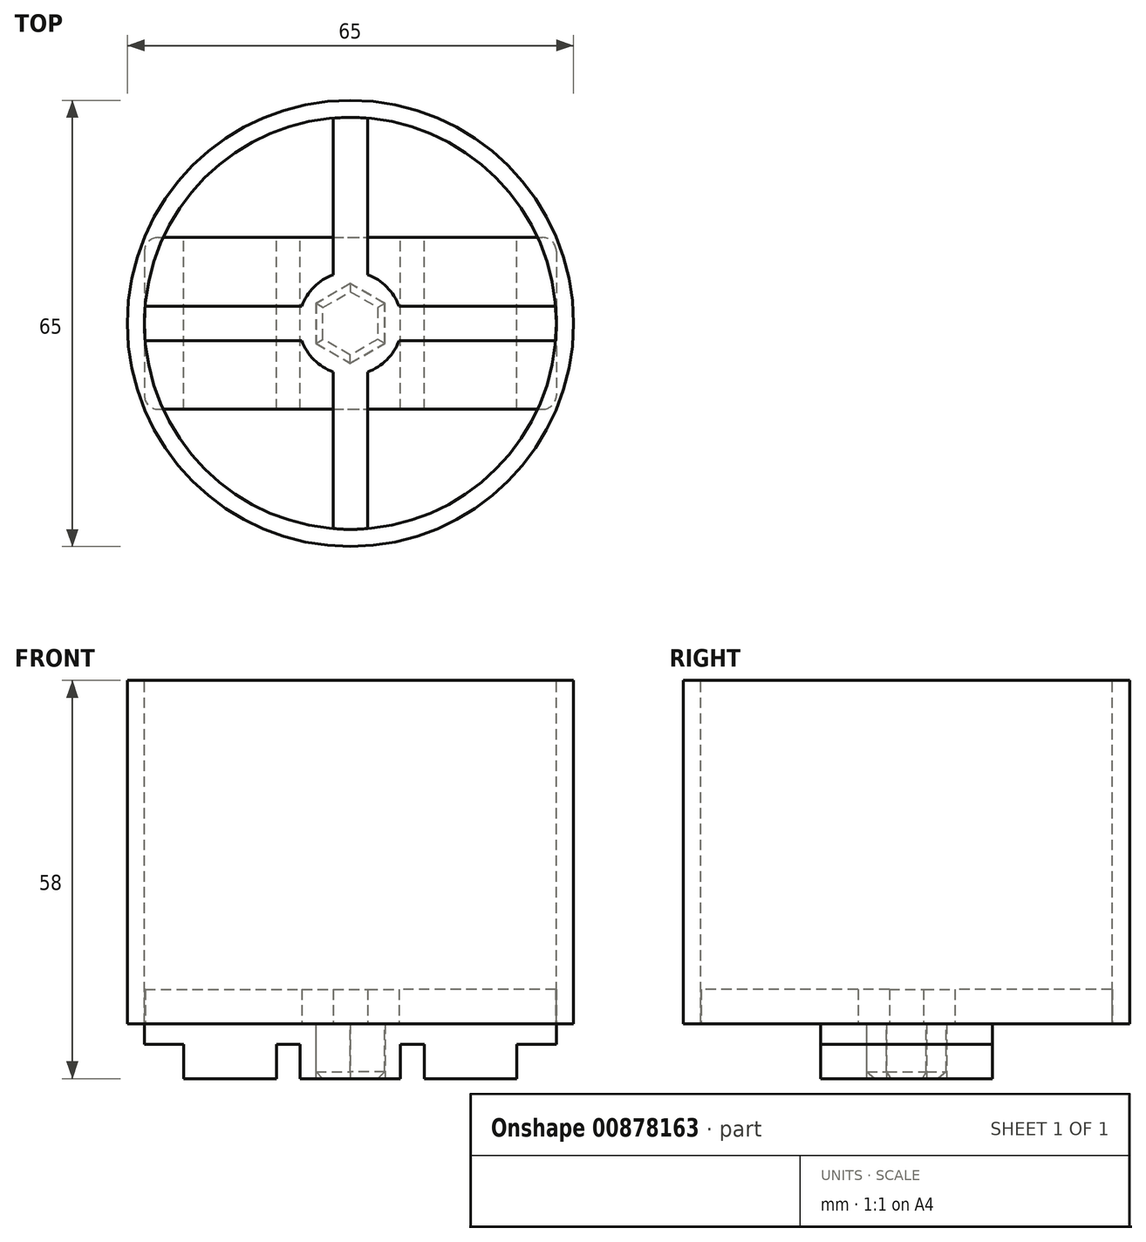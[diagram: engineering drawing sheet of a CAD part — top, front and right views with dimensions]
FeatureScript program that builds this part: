
annotation { "Feature Type Name" : "Feature", "Feature Type Description" : "" }
export const myFeature = defineFeature(function(context is Context, id is Id, definition is map)
    precondition{}
    {
        {
            var Q0;
            Q0=qCreatedBy(makeId("Top.planeOp"),FACE);
            var sketch = newSketch(context, id + "F0", { "sketchPlane" : qUnion([Q0])});
            skLineSegment(sketch, "E0.bottom", {"start": v(-30, 12.5) * mm, "end": v(30, 12.5) * mm});
            skLineSegment(sketch, "E0.top", {"start": v(-30, -12.5) * mm, "end": v(30, -12.5) * mm});
            skLineSegment(sketch, "E0.left", {"start": v(-30, 12.5) * mm, "end": v(-30, -12.5) * mm});
            skLineSegment(sketch, "E0.right", {"start": v(30, 12.5) * mm, "end": v(30, -12.5) * mm});
            skPoint(sketch, "E1", {"position": v(-30, 0) * mm});
            skPoint(sketch, "E2", {"position": v(0, 12.5) * mm});
            skSolve(sketch);
        }
        {
            var Q0;
            Q0=makeQuery(id+"F0.imprint","IMPRINT",FACE,{"disambiguationData":[TD([[makeQuery(id+"F0.imprint","IMPRINT",EDGE,{"derivedFrom":sQuery(id+"F0.wireOp",EDGE,"E0.bottom")}),-1.0]])]});
            extrude(context, id + "F1", {"entities" : qUnion([Q0]), "oppositeDirection" : true, "depth" : 8 * mm, "offsetDistance" : 25 * mm});
        }
        {
            var Q0;
            Q0=makeQuery(id+"F1.opExtrude","CAP_FACE",FACE,{"disambiguationData":[OSD([sQuery(id+"F0.wireOp",EDGE,"E0.bottom"),sQuery(id+"F0.wireOp",EDGE,"E0.top"),sQuery(id+"F0.wireOp",EDGE,"E0.left"),sQuery(id+"F0.wireOp",EDGE,"E0.right")])],"isStart":false});
            var sketch = newSketch(context, id + "F2", { "sketchPlane" : qUnion([Q0])});
            skLineSegment(sketch, "E3.bottom", {"start": v(-24.25, 12.5) * mm, "end": v(-10.75, 12.5) * mm});
            skLineSegment(sketch, "E3.top", {"start": v(-24.25, -12.5) * mm, "end": v(-10.75, -12.5) * mm});
            skLineSegment(sketch, "E3.left", {"start": v(-24.25, 12.5) * mm, "end": v(-24.25, -12.5) * mm});
            skLineSegment(sketch, "E3.right", {"start": v(-10.75, 12.5) * mm, "end": v(-10.75, -12.5) * mm});
            skLineSegment(sketch, "E4.bottom", {"start": v(-7.3, 12.5) * mm, "end": v(7.3, 12.5) * mm});
            skLineSegment(sketch, "E4.top", {"start": v(-7.3, -12.5) * mm, "end": v(7.3, -12.5) * mm});
            skLineSegment(sketch, "E4.left", {"start": v(-7.3, 12.5) * mm, "end": v(-7.3, -12.5) * mm});
            skLineSegment(sketch, "E4.right", {"start": v(7.3, 12.5) * mm, "end": v(7.3, -12.5) * mm});
            skLineSegment(sketch, "E5.bottom", {"start": v(10.75, 12.5) * mm, "end": v(24.25, 12.5) * mm});
            skLineSegment(sketch, "E5.top", {"start": v(10.75, -12.5) * mm, "end": v(24.25, -12.5) * mm});
            skLineSegment(sketch, "E5.left", {"start": v(10.75, 12.5) * mm, "end": v(10.75, -12.5) * mm});
            skLineSegment(sketch, "E5.right", {"start": v(24.25, 12.5) * mm, "end": v(24.25, -12.5) * mm});
            skPoint(sketch, "E6", {"position": v(0, 12.5) * mm});
            skLineSegment(sketch, "E7", {"start": v(-10.75, 12.5) * mm, "end": v(-7.3, 12.5) * mm, "construction": true});
            skLineSegment(sketch, "E8", {"start": v(7.3, 12.5) * mm, "end": v(10.75, 12.5) * mm, "construction": true});
            skSolve(sketch);
        }
        {
            var Q0;
            {var subQ0=sQuery(id+"F2.wireOp",EDGE,"E3.left");Q0=makeQuery(id+"F2.imprint","IMPRINT",FACE,{"disambiguationData":[TD([[makeQuery(id+"F2.imprint","IMPRINT",EDGE,{"derivedFrom":subQ0}),-1.0]])]});}
            var Q1;
            {var subQ0=sQuery(id+"F2.wireOp",EDGE,"E3.right");Q1=makeQuery(id+"F2.imprint","IMPRINT",FACE,{"disambiguationData":[TD([[makeQuery(id+"F2.imprint","IMPRINT",EDGE,{"derivedFrom":subQ0}),1.0]])]});}
            var Q2;
            {var subQ0=sQuery(id+"F2.wireOp",EDGE,"E4.right");Q2=makeQuery(id+"F2.imprint","IMPRINT",FACE,{"disambiguationData":[TD([[makeQuery(id+"F2.imprint","IMPRINT",EDGE,{"derivedFrom":subQ0}),1.0]])]});}
            var Q3;
            {var subQ0=sQuery(id+"F2.wireOp",EDGE,"E5.right");Q3=makeQuery(id+"F2.imprint","IMPRINT",FACE,{"disambiguationData":[TD([[makeQuery(id+"F2.imprint","IMPRINT",EDGE,{"derivedFrom":subQ0}),1.0]])]});}
            extrude(context, id + "F3", {"entities" : qUnion([Q0, Q1, Q2, Q3]), "operationType" : NewBodyOperationType.REMOVE, "oppositeDirection" : true, "depth" : 5 * mm, "offsetDistance" : 25 * mm});
        }
        {
            var Q0;
            {var subQ0=sQuery(id+"F0.wireOp",EDGE,"E0.bottom");var subQ1=sQuery(id+"F0.wireOp",EDGE,"E0.top");Q0=makeQuery(id+"F3.boolean.opBoolean","SPLIT",FACE,{"disambiguationData":[TD([makeQuery(id+"F3.opExtrude","SWEPT_FACE",FACE,{"disambiguationData":[OSD([sQuery(id+"F2.wireOp",EDGE,"E4.left")])]})])],"derivedFrom":makeQuery(id+"F1.opExtrude","CAP_FACE",FACE,{"disambiguationData":[OSD([subQ0,subQ1,sQuery(id+"F0.wireOp",EDGE,"E0.left"),sQuery(id+"F0.wireOp",EDGE,"E0.right")])],"isStart":false})});}
            var sketch = newSketch(context, id + "F4", { "sketchPlane" : qUnion([Q0])});
            skCircle(sketch, "E9.cCircle", {"center": v(0, 0) * mm, "radius": 5.05 * mm, "construction": true});
            skLineSegment(sketch, "E9.0", {"start": v(5.05, -2.92) * mm, "end": v(0, -5.83) * mm});
            skLineSegment(sketch, "E9.1", {"start": v(0, -5.83) * mm, "end": v(-5.05, -2.92) * mm});
            skLineSegment(sketch, "E9.2", {"start": v(-5.05, -2.92) * mm, "end": v(-5.05, 2.92) * mm});
            skLineSegment(sketch, "E9.3", {"start": v(-5.05, 2.92) * mm, "end": v(0, 5.83) * mm});
            skLineSegment(sketch, "E9.4", {"start": v(0, 5.83) * mm, "end": v(5.05, 2.92) * mm});
            skLineSegment(sketch, "E9.5", {"start": v(5.05, 2.92) * mm, "end": v(5.05, -2.92) * mm});
            skPoint(sketch, "E9.0.midPoint", {"position": v(2.53, -4.37) * mm});
            skSolve(sketch);
        }
        {
            var Q0;
            Q0=makeQuery(id+"F4.imprint","IMPRINT",FACE,{"disambiguationData":[TD([[makeQuery(id+"F4.imprint","IMPRINT",EDGE,{"derivedFrom":sQuery(id+"F4.wireOp",EDGE,"E9.0")}),-1.0]])]});
            extrude(context, id + "F5", {"entities" : qUnion([Q0]), "operationType" : NewBodyOperationType.REMOVE, "endBound" : BoundingType.UP_TO_NEXT, "oppositeDirection" : true, "depth" : 25 * mm, "offsetDistance" : 25 * mm});
        }
        {
            var Q0;
            Q0=qCreatedBy(makeId("Top.planeOp"),FACE);
            var sketch = newSketch(context, id + "F6", { "sketchPlane" : qUnion([Q0])});
            skCircle(sketch, "E10", {"center": v(0, 0) * mm, "radius": 32.5 * mm});
            skSolve(sketch);
        }
        {
            var Q0;
            Q0 = qSketchRegion(id + "F6", true);
            extrude(context, id + "F7", {"entities" : qUnion([Q0]), "depth" : 50 * mm, "offsetDistance" : 25 * mm});
        }
        {
            var Q0;
            Q0=makeQuery(id+"F7.opExtrude","CAP_FACE",FACE,{"disambiguationData":[OSD([sQuery(id+"F6.wireOp",EDGE,"E10")])],"isStart":false});
            var sketch = newSketch(context, id + "F8", { "sketchPlane" : qUnion([Q0])});
            skCircle(sketch, "E11", {"center": v(0, 0) * mm, "radius": 30 * mm});
            skSolve(sketch);
        }
        {
            var Q0;
            Q0=makeQuery(id+"F8.imprint","IMPRINT",FACE,{"disambiguationData":[TD([[makeQuery(id+"F8.imprint","IMPRINT",EDGE,{"derivedFrom":sQuery(id+"F8.wireOp",EDGE,"E11")}),1.0]])]});
            extrude(context, id + "F9", {"entities" : qUnion([Q0]), "operationType" : NewBodyOperationType.REMOVE, "endBound" : BoundingType.UP_TO_NEXT, "oppositeDirection" : true, "depth" : 25 * mm, "offsetDistance" : 25 * mm});
        }
        {
            var Q0;
            Q0=qCreatedBy(makeId("Top.planeOp"),FACE);
            var sketch = newSketch(context, id + "F10", { "sketchPlane" : qUnion([Q0])});
            skArc(sketch, "E12.0", {"start": v(-29.9, 2.5) * mm, "mid": v(-30, 0) * mm, "end": v(-29.9, -2.5) * mm});
            skLineSegment(sketch, "E13", {"start": v(-2.5, 29.9) * mm, "end": v(-2.5, 2.5) * mm});
            skLineSegment(sketch, "E14", {"start": v(-2.5, 2.5) * mm, "end": v(-29.9, 2.5) * mm});
            skLineSegment(sketch, "E15", {"start": v(-29.9, -2.5) * mm, "end": v(-2.5, -2.5) * mm});
            skLineSegment(sketch, "E16", {"start": v(-2.5, -2.5) * mm, "end": v(-2.5, -29.9) * mm});
            skLineSegment(sketch, "E17", {"start": v(2.5, 29.9) * mm, "end": v(2.5, 2.5) * mm});
            skLineSegment(sketch, "E18", {"start": v(2.5, 2.5) * mm, "end": v(29.9, 2.5) * mm});
            skLineSegment(sketch, "E19", {"start": v(29.9, -2.5) * mm, "end": v(2.5, -2.5) * mm});
            skLineSegment(sketch, "E20", {"start": v(2.5, -2.5) * mm, "end": v(2.5, -29.9) * mm});
            skCircle(sketch, "E21", {"center": v(0, 0) * mm, "radius": 7.5 * mm});
            skArc(sketch, "E22.trimOffspring", {"start": v(2.5, 29.9) * mm, "mid": v(0, 30) * mm, "end": v(-2.5, 29.9) * mm});
            skArc(sketch, "E23.trimOffspring", {"start": v(-2.5, -29.9) * mm, "mid": v(0, -30) * mm, "end": v(2.5, -29.9) * mm});
            skArc(sketch, "E24.trimOffspring", {"start": v(29.9, -2.5) * mm, "mid": v(30, 0) * mm, "end": v(29.9, 2.5) * mm});
            skPoint(sketch, "E25", {"position": v(-7.07, 2.5) * mm});
            skPoint(sketch, "E26", {"position": v(-7.07, -2.5) * mm});
            skPoint(sketch, "E27", {"position": v(-2.5, -7.07) * mm});
            skSolve(sketch);
        }
        {
            var Q0;
            {var subQ1=sQuery(id+"F10.wireOp",EDGE,"E14");var subQ14=sQuery(id+"F10.wireOp",EDGE,"E13");var subQ15=makeQuery(id+"F10.imprint","INTERSECT",VERTEX,{"derivedFrom":[subQ14,subQ1]});Q0=makeQuery(id+"F10.imprint","IMPRINT",FACE,{"disambiguationData":[TD([[makeQuery(id+"F10.imprint","IMPRINT",EDGE,{"disambiguationData":[TD([[subQ15,1.0]])],"derivedFrom":subQ14}),1.0]])]});}
            var Q1;
            {var subQ0=sQuery(id+"F10.wireOp",EDGE,"E12.0");Q1=makeQuery(id+"F10.imprint","IMPRINT",FACE,{"disambiguationData":[TD([[makeQuery(id+"F10.imprint","IMPRINT",EDGE,{"derivedFrom":subQ0}),1.0]])]});}
            var Q2;
            {var subQ0=sQuery(id+"F10.wireOp",EDGE,"E24.trimOffspring");Q2=makeQuery(id+"F10.imprint","IMPRINT",FACE,{"disambiguationData":[TD([[makeQuery(id+"F10.imprint","IMPRINT",EDGE,{"derivedFrom":subQ0}),1.0]])]});}
            var Q3;
            {var subQ0=sQuery(id+"F10.wireOp",EDGE,"E23.trimOffspring");Q3=makeQuery(id+"F10.imprint","IMPRINT",FACE,{"disambiguationData":[TD([[makeQuery(id+"F10.imprint","IMPRINT",EDGE,{"derivedFrom":subQ0}),1.0]])]});}
            var Q4;
            {var subQ0=sQuery(id+"F10.wireOp",EDGE,"E22.trimOffspring");Q4=makeQuery(id+"F10.imprint","IMPRINT",FACE,{"disambiguationData":[TD([[makeQuery(id+"F10.imprint","IMPRINT",EDGE,{"derivedFrom":subQ0}),1.0]])]});}
            var Q5;
            {var subQ0=sQuery(id+"F10.wireOp",EDGE,"E14");var subQ1=sQuery(id+"F10.wireOp",EDGE,"E13");var subQ2=makeQuery(id+"F10.imprint","INTERSECT",VERTEX,{"derivedFrom":[subQ1,subQ0]});Q5=makeQuery(id+"F10.imprint","IMPRINT",FACE,{"disambiguationData":[TD([[makeQuery(id+"F10.imprint","IMPRINT",EDGE,{"disambiguationData":[TD([[subQ2,1.0]])],"derivedFrom":subQ1}),-1.0]])]});}
            var Q6;
            {var subQ0=sQuery(id+"F10.wireOp",EDGE,"E18");var subQ1=sQuery(id+"F10.wireOp",EDGE,"E17");var subQ2=makeQuery(id+"F10.imprint","INTERSECT",VERTEX,{"derivedFrom":[subQ1,subQ0]});Q6=makeQuery(id+"F10.imprint","IMPRINT",FACE,{"disambiguationData":[TD([[makeQuery(id+"F10.imprint","IMPRINT",EDGE,{"disambiguationData":[TD([[subQ2,1.0]])],"derivedFrom":subQ1}),1.0]])]});}
            var Q7;
            {var subQ0=sQuery(id+"F10.wireOp",EDGE,"E20");var subQ1=sQuery(id+"F10.wireOp",EDGE,"E19");var subQ2=makeQuery(id+"F10.imprint","INTERSECT",VERTEX,{"derivedFrom":[subQ1,subQ0]});Q7=makeQuery(id+"F10.imprint","IMPRINT",FACE,{"disambiguationData":[TD([[makeQuery(id+"F10.imprint","IMPRINT",EDGE,{"disambiguationData":[TD([[subQ2,1.0]])],"derivedFrom":subQ1}),1.0]])]});}
            var Q8;
            {var subQ0=sQuery(id+"F10.wireOp",EDGE,"E16");var subQ1=sQuery(id+"F10.wireOp",EDGE,"E15");var subQ2=makeQuery(id+"F10.imprint","INTERSECT",VERTEX,{"derivedFrom":[subQ1,subQ0]});Q8=makeQuery(id+"F10.imprint","IMPRINT",FACE,{"disambiguationData":[TD([[makeQuery(id+"F10.imprint","IMPRINT",EDGE,{"disambiguationData":[TD([[subQ2,1.0]])],"derivedFrom":subQ1}),-1.0]])]});}
            extrude(context, id + "F11", {"entities" : qUnion([Q0, Q1, Q2, Q3, Q4, Q5, Q6, Q7, Q8]), "depth" : 5 * mm, "offsetDistance" : 25 * mm});
        }
        {
            var Q0;
            Q0=makeQuery(id+"F11.opExtrude","CAP_FACE",FACE,{"disambiguationData":[OSD([sQuery(id+"F10.wireOp",EDGE,"E12.0"),sQuery(id+"F10.wireOp",EDGE,"E13"),sQuery(id+"F10.wireOp",EDGE,"E14"),sQuery(id+"F10.wireOp",EDGE,"E15"),sQuery(id+"F10.wireOp",EDGE,"E16"),sQuery(id+"F10.wireOp",EDGE,"E17"),sQuery(id+"F10.wireOp",EDGE,"E18"),sQuery(id+"F10.wireOp",EDGE,"E19"),sQuery(id+"F10.wireOp",EDGE,"E20"),sQuery(id+"F10.wireOp",EDGE,"E21"),sQuery(id+"F10.wireOp",EDGE,"E22.trimOffspring"),sQuery(id+"F10.wireOp",EDGE,"E23.trimOffspring"),sQuery(id+"F10.wireOp",EDGE,"E24.trimOffspring")])],"isStart":true});
            var sketch = newSketch(context, id + "F12", { "sketchPlane" : qUnion([Q0])});
            skCircle(sketch, "E28.cCircle", {"center": v(0, 0) * mm, "radius": 5 * mm, "construction": true});
            skLineSegment(sketch, "E28.0", {"start": v(5, -2.89) * mm, "end": v(0, -5.77) * mm});
            skLineSegment(sketch, "E28.1", {"start": v(0, -5.77) * mm, "end": v(-5, -2.89) * mm});
            skLineSegment(sketch, "E28.2", {"start": v(-5, -2.89) * mm, "end": v(-5, 2.89) * mm});
            skLineSegment(sketch, "E28.3", {"start": v(-5, 2.89) * mm, "end": v(0, 5.77) * mm});
            skLineSegment(sketch, "E28.4", {"start": v(0, 5.77) * mm, "end": v(5, 2.89) * mm});
            skLineSegment(sketch, "E28.5", {"start": v(5, 2.89) * mm, "end": v(5, -2.89) * mm});
            skPoint(sketch, "E28.0.midPoint", {"position": v(2.5, -4.33) * mm});
            skSolve(sketch);
        }
        {
            var Q0;
            Q0=makeQuery(id+"F12.imprint","IMPRINT",FACE,{"disambiguationData":[TD([[makeQuery(id+"F12.imprint","IMPRINT",EDGE,{"derivedFrom":sQuery(id+"F12.wireOp",EDGE,"E28.0")}),-1.0]])]});
            extrude(context, id + "F13", {"entities" : qUnion([Q0]), "operationType" : NewBodyOperationType.ADD, "depth" : 8 * mm, "offsetDistance" : 25 * mm});
        }
        {
            var Q0;
            Q0=makeQuery(id+"F13.opExtrude","CAP_FACE",FACE,{"disambiguationData":[OSD([sQuery(id+"F12.wireOp",EDGE,"E28.0"),sQuery(id+"F12.wireOp",EDGE,"E28.1"),sQuery(id+"F12.wireOp",EDGE,"E28.2"),sQuery(id+"F12.wireOp",EDGE,"E28.3"),sQuery(id+"F12.wireOp",EDGE,"E28.4"),sQuery(id+"F12.wireOp",EDGE,"E28.5")])],"isStart":false});
            chamfer(context, id + "F14", {"entities" : qUnion([Q0]), "width" : 1 * mm, "tangentPropagation" : true});
        }
        {
            var Q0;
            Q0=makeQuery(id+"F1.opExtrude","SWEPT_EDGE",EDGE,{"disambiguationData":[OSD([sQuery(id+"F0.wireOp",EDGE,"E0.bottom"),sQuery(id+"F0.wireOp",EDGE,"E0.right")])]});
            var Q1;
            Q1=makeQuery(id+"F1.opExtrude","SWEPT_EDGE",EDGE,{"disambiguationData":[OSD([sQuery(id+"F0.wireOp",EDGE,"E0.bottom"),sQuery(id+"F0.wireOp",EDGE,"E0.left")])]});
            var Q2;
            Q2=makeQuery(id+"F1.opExtrude","SWEPT_EDGE",EDGE,{"disambiguationData":[OSD([sQuery(id+"F0.wireOp",EDGE,"E0.top"),sQuery(id+"F0.wireOp",EDGE,"E0.left")])]});
            var Q3;
            Q3=makeQuery(id+"F1.opExtrude","SWEPT_EDGE",EDGE,{"disambiguationData":[OSD([sQuery(id+"F0.wireOp",EDGE,"E0.top"),sQuery(id+"F0.wireOp",EDGE,"E0.right")])]});
            fillet(context, id + "F15", {"entities" : qUnion([Q0, Q1, Q2, Q3]), "radius" : 2 * mm, "tangentPropagation" : true, "allowEdgeOverflow" : false});
        }
    });
